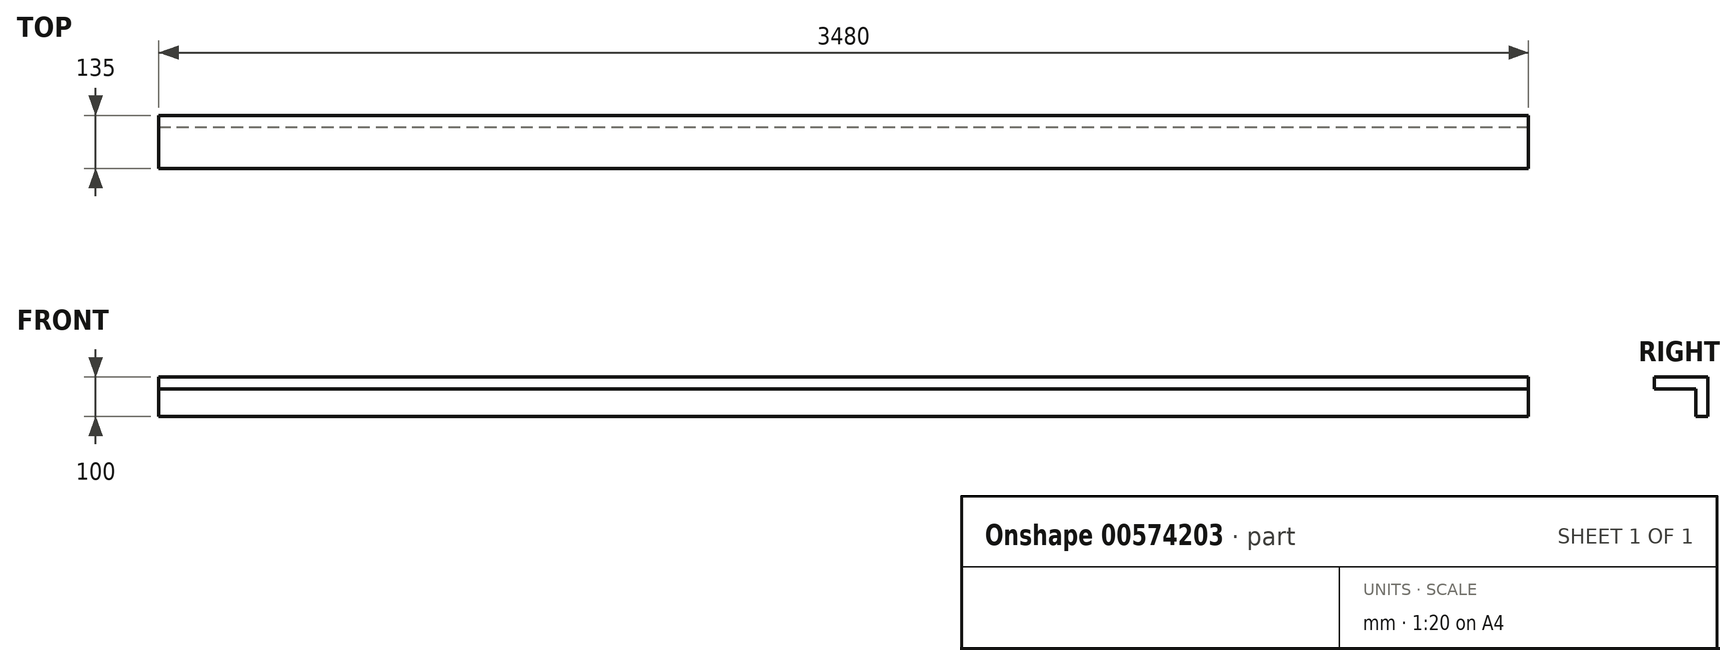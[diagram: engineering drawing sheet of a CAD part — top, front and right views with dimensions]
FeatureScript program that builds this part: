
annotation { "Feature Type Name" : "Feature", "Feature Type Description" : "" }
export const myFeature = defineFeature(function(context is Context, id is Id, definition is map)
    precondition{}
    {
        {
            var Q0;
            Q0=qCreatedBy(makeId("Top.planeOp"),FACE);
            var sketch = newSketch(context, id + "F0", { "sketchPlane" : qUnion([Q0])});
            skLineSegment(sketch, "E0.bottom", {"start": v(90, -85) * mm, "end": v(-3390, -85) * mm});
            skLineSegment(sketch, "E0.top", {"start": v(90, 50) * mm, "end": v(-3390, 50) * mm});
            skLineSegment(sketch, "E0.left", {"start": v(90, -85) * mm, "end": v(90, 50) * mm});
            skLineSegment(sketch, "E0.right", {"start": v(-3390, -85) * mm, "end": v(-3390, 50) * mm});
            skSolve(sketch);
        }
        {
            var Q0;
            Q0=makeQuery(id+"F0.imprint","IMPRINT",FACE,{"disambiguationData":[TD([[makeQuery(id+"F0.imprint","IMPRINT",EDGE,{"derivedFrom":sQuery(id+"F0.wireOp",EDGE,"E0.bottom")}),-1.0]])]});
            extrude(context, id + "F1", {"entities" : qUnion([Q0]), "depth" : 30 * mm, "offsetDistance" : 25 * mm});
        }
        {
            var Q0;
            Q0=makeQuery(id+"F1.opExtrude","SWEPT_FACE",FACE,{"disambiguationData":[OSD([sQuery(id+"F0.wireOp",EDGE,"E0.left")])]});
            var sketch = newSketch(context, id + "F2", { "sketchPlane" : qUnion([Q0])});
            skLineSegment(sketch, "E1.bottom", {"start": v(50, 0) * mm, "end": v(20, 0) * mm});
            skLineSegment(sketch, "E1.top", {"start": v(50, -70) * mm, "end": v(20, -70) * mm});
            skLineSegment(sketch, "E1.left", {"start": v(50, 0) * mm, "end": v(50, -70) * mm});
            skLineSegment(sketch, "E1.right", {"start": v(20, 0) * mm, "end": v(20, -70) * mm});
            skSolve(sketch);
        }
        {
            var Q0;
            Q0=makeQuery(id+"F2.imprint","IMPRINT",FACE,{"disambiguationData":[TD([[makeQuery(id+"F2.imprint","IMPRINT",EDGE,{"derivedFrom":sQuery(id+"F2.wireOp",EDGE,"E1.bottom")}),-1.0]])]});
            extrude(context, id + "F3", {"entities" : qUnion([Q0]), "operationType" : NewBodyOperationType.ADD, "oppositeDirection" : true, "depth" : 3480 * mm, "offsetDistance" : 25 * mm});
        }
    });
